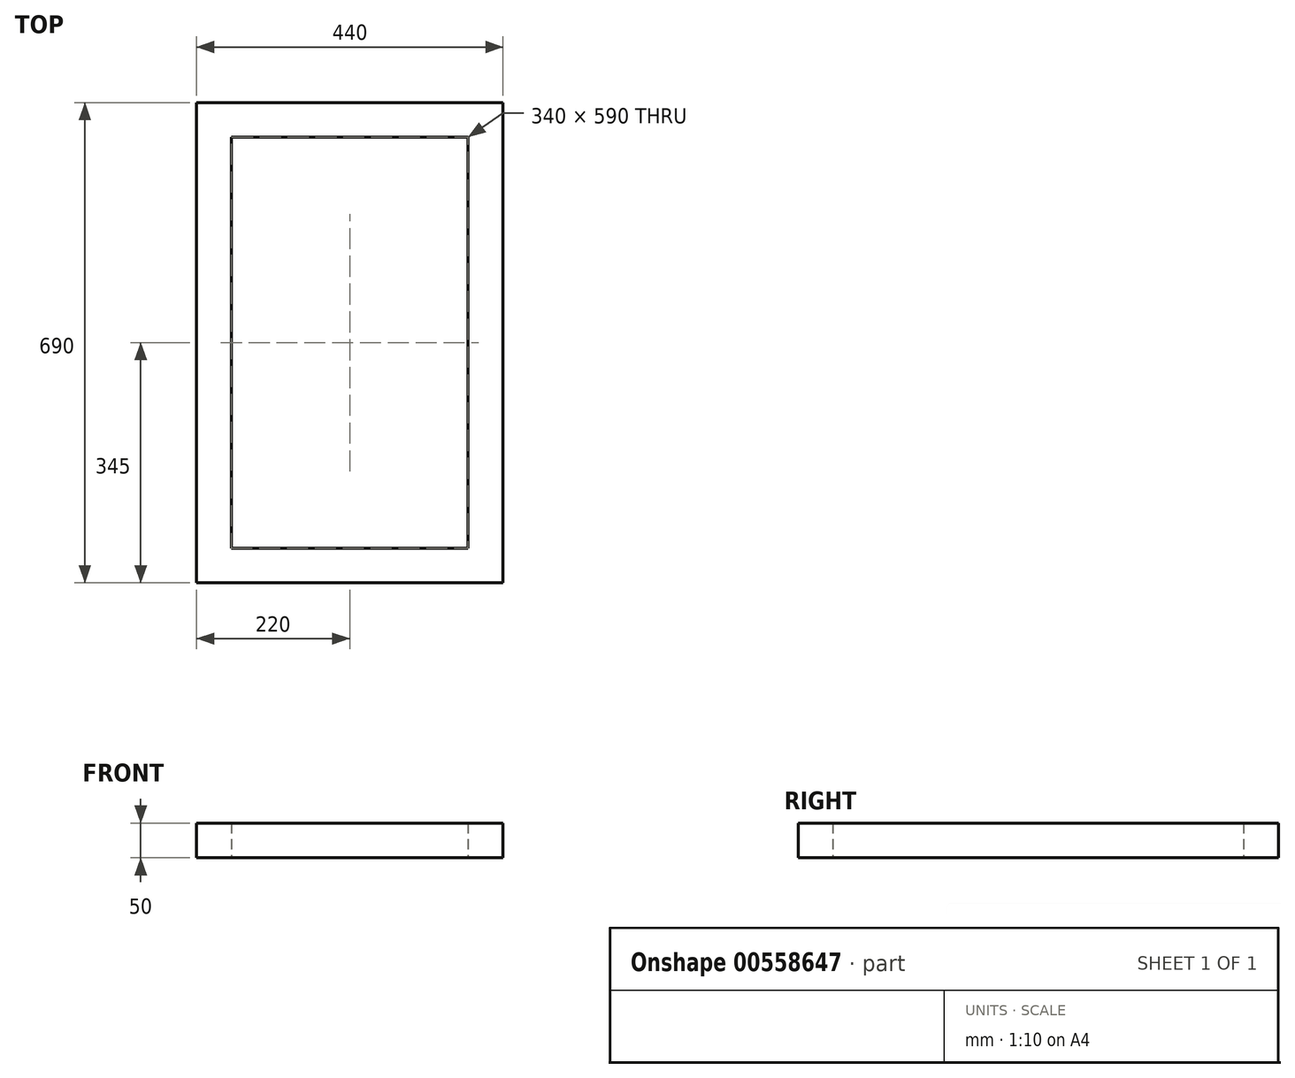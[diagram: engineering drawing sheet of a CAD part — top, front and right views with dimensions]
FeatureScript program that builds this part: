
annotation { "Feature Type Name" : "Feature", "Feature Type Description" : "" }
export const myFeature = defineFeature(function(context is Context, id is Id, definition is map)
    precondition{}
    {
        {
            var Q0;
            Q0=qCreatedBy(makeId("Top.planeOp"),FACE);
            var sketch = newSketch(context, id + "F0", { "sketchPlane" : qUnion([Q0])});
            skLineSegment(sketch, "E0.bottom", {"start": v(0, 0) * mm, "end": v(350, 0) * mm, "construction": true});
            skLineSegment(sketch, "E0.top", {"start": v(0, 600) * mm, "end": v(350, 600) * mm, "construction": true});
            skLineSegment(sketch, "E0.left", {"start": v(0, 0) * mm, "end": v(0, 600) * mm, "construction": true});
            skLineSegment(sketch, "E0.right", {"start": v(350, 0) * mm, "end": v(350, 600) * mm, "construction": true});
            skLineSegment(sketch, "E1.bottom", {"start": v(5, 595) * mm, "end": v(345, 595) * mm});
            skLineSegment(sketch, "E1.top", {"start": v(5, 5) * mm, "end": v(345, 5) * mm});
            skLineSegment(sketch, "E1.left", {"start": v(5, 595) * mm, "end": v(5, 5) * mm});
            skLineSegment(sketch, "E1.right", {"start": v(345, 595) * mm, "end": v(345, 5) * mm});
            skLineSegment(sketch, "E2.bottom", {"start": v(-45, 645) * mm, "end": v(395, 645) * mm});
            skLineSegment(sketch, "E2.top", {"start": v(-45, -45) * mm, "end": v(395, -45) * mm});
            skLineSegment(sketch, "E2.left", {"start": v(-45, 645) * mm, "end": v(-45, -45) * mm});
            skLineSegment(sketch, "E2.right", {"start": v(395, 645) * mm, "end": v(395, -45) * mm});
            skSolve(sketch);
        }
        {
            var Q0;
            Q0=makeQuery(id+"F0.imprint","IMPRINT",FACE,{"disambiguationData":[TD([[makeQuery(id+"F0.imprint","IMPRINT",EDGE,{"derivedFrom":sQuery(id+"F0.wireOp",EDGE,"E1.bottom")}),1.0]])]});
            extrude(context, id + "F1", {"entities" : qUnion([Q0]), "depth" : 50 * mm, "offsetDistance" : 25 * mm});
        }
    });
